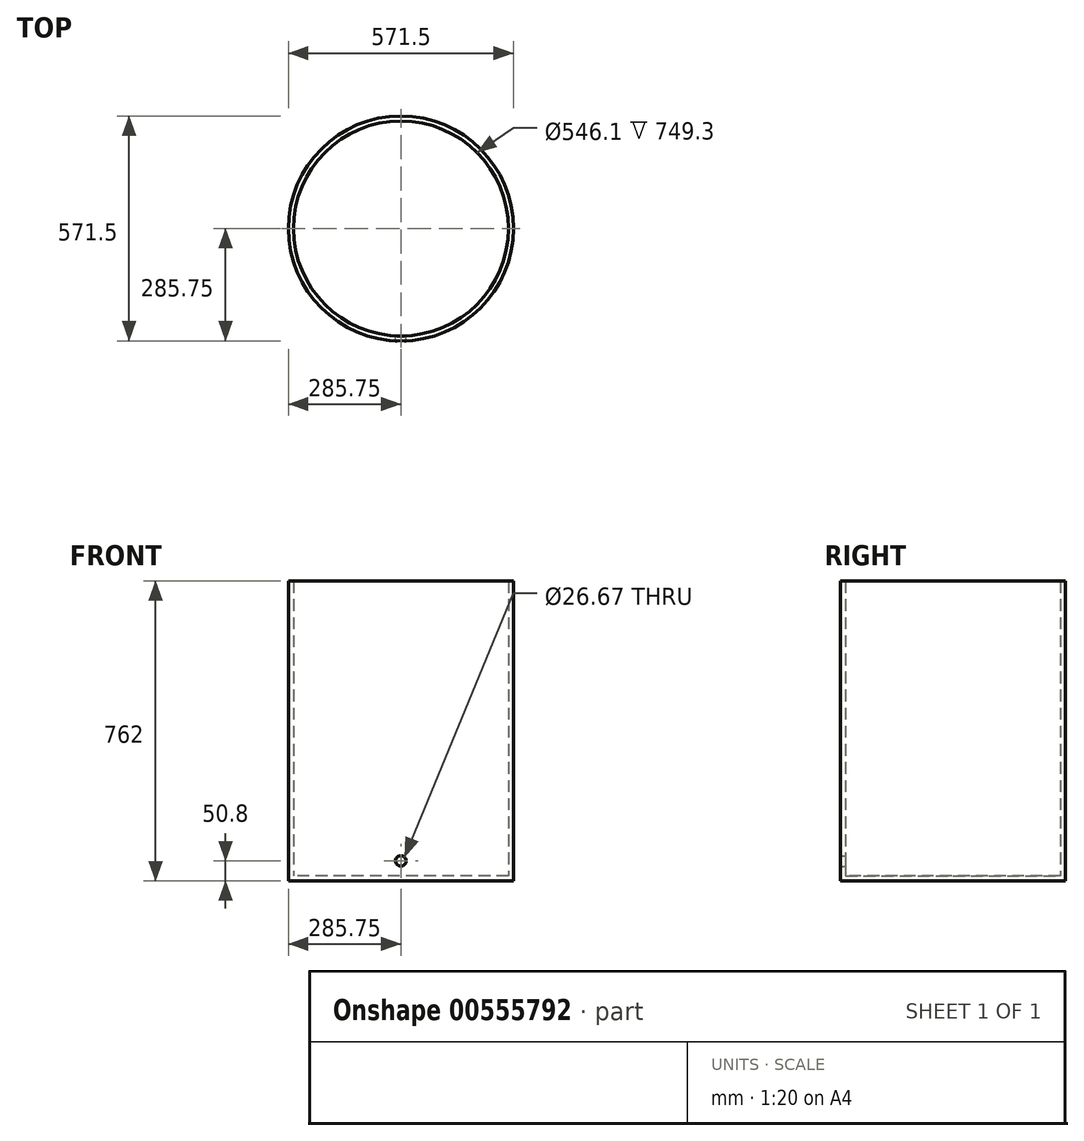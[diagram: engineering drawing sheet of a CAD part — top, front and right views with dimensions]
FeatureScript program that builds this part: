
annotation { "Feature Type Name" : "Feature", "Feature Type Description" : "" }
export const myFeature = defineFeature(function(context is Context, id is Id, definition is map)
    precondition{}
    {
        {
            var Q0;
            Q0=qCreatedBy(makeId("Top.planeOp"),FACE);
            var sketch = newSketch(context, id + "F0", { "sketchPlane" : qUnion([Q0])});
            skCircle(sketch, "E0", {"center": v(0, 0) * mm, "radius": 285.75 * mm});
            skSolve(sketch);
        }
        {
            var Q0;
            Q0 = qSketchRegion(id + "F0", true);
            extrude(context, id + "F1", {"entities" : qUnion([Q0]), "depth" : 762 * mm, "offsetDistance" : 25.4 * mm});
        }
        {
            var Q0;
            Q0=makeQuery(id+"F1.opExtrude","CAP_FACE",FACE,{"disambiguationData":[OSD([sQuery(id+"F0.wireOp",EDGE,"E0")])],"isStart":false});
            shell(context, id + "F2", {"entities" : qUnion([Q0]), "thickness" : 12.7 * mm});
        }
        {
            var Q0;
            Q0=qCreatedBy(makeId("Front.planeOp"),FACE);
            var sketch = newSketch(context, id + "F3", { "sketchPlane" : qUnion([Q0])});
            skLineSegment(sketch, "E1", {"start": v(0, 0) * mm, "end": v(0, 101.6) * mm, "construction": true});
            skCircle(sketch, "E2", {"center": v(0, 50.8) * mm, "radius": 13.34 * mm});
            skSolve(sketch);
        }
        {
            var Q0;
            Q0 = qSketchRegion(id + "F3", true);
            extrude(context, id + "F4", {"entities" : qUnion([Q0]), "operationType" : NewBodyOperationType.REMOVE, "depth" : 327.66 * mm, "offsetDistance" : 25.4 * mm});
        }
    });
